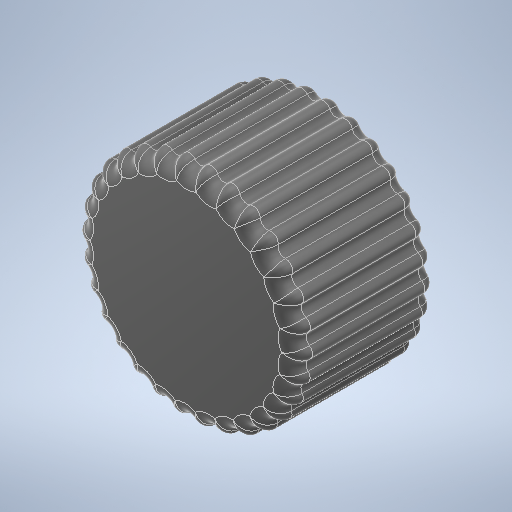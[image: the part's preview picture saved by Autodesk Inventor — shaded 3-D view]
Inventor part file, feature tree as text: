
AUTODESK INVENTOR PART (.ipt)
format: ipt  version: 2025.1 (Build 291241020, 241B)  size: 2,318,336 bytes
history: native  units: mm
features: fillet x2, sketch x2, revolve x1, extrude x1, pattern_circular x1
ambient origin geometry x8: Origin, YZ Plane, XZ Plane, XY Plane, X Axis, Y Axis, Z Axis, Center Point
bodies: Solid1 (feature_tree)
feature tree (7):
  revolve  "Revolution1"  [1 undecoded]
  extrude  "Extrusion1"  Depth=5.0mm
  fillet  "Fillet1"  [1 undecoded]
  pattern_circular  "Circular Pattern1"  [2 undecoded]
  fillet  "Fillet2"  Radius=14.0mm
  sketch  "Sketch1"  dims[d0=16.15mm d1=10.2mm]
  sketch  "Sketch2"  dims[d2=20.0mm d3=5.0mm d4=360.0deg d5=1.2mm d6=14.0mm d7=16.5mm d8=0.0mm d9=0.0mm d10=1.0mm d11=300.0mm d12=360.0deg d14=2.0mm]
note: 4 required parameter values undecoded (feature->parameter linkage not recoverable at this tier; creation-order binding heuristic only, values carry confidence <= 0.55)